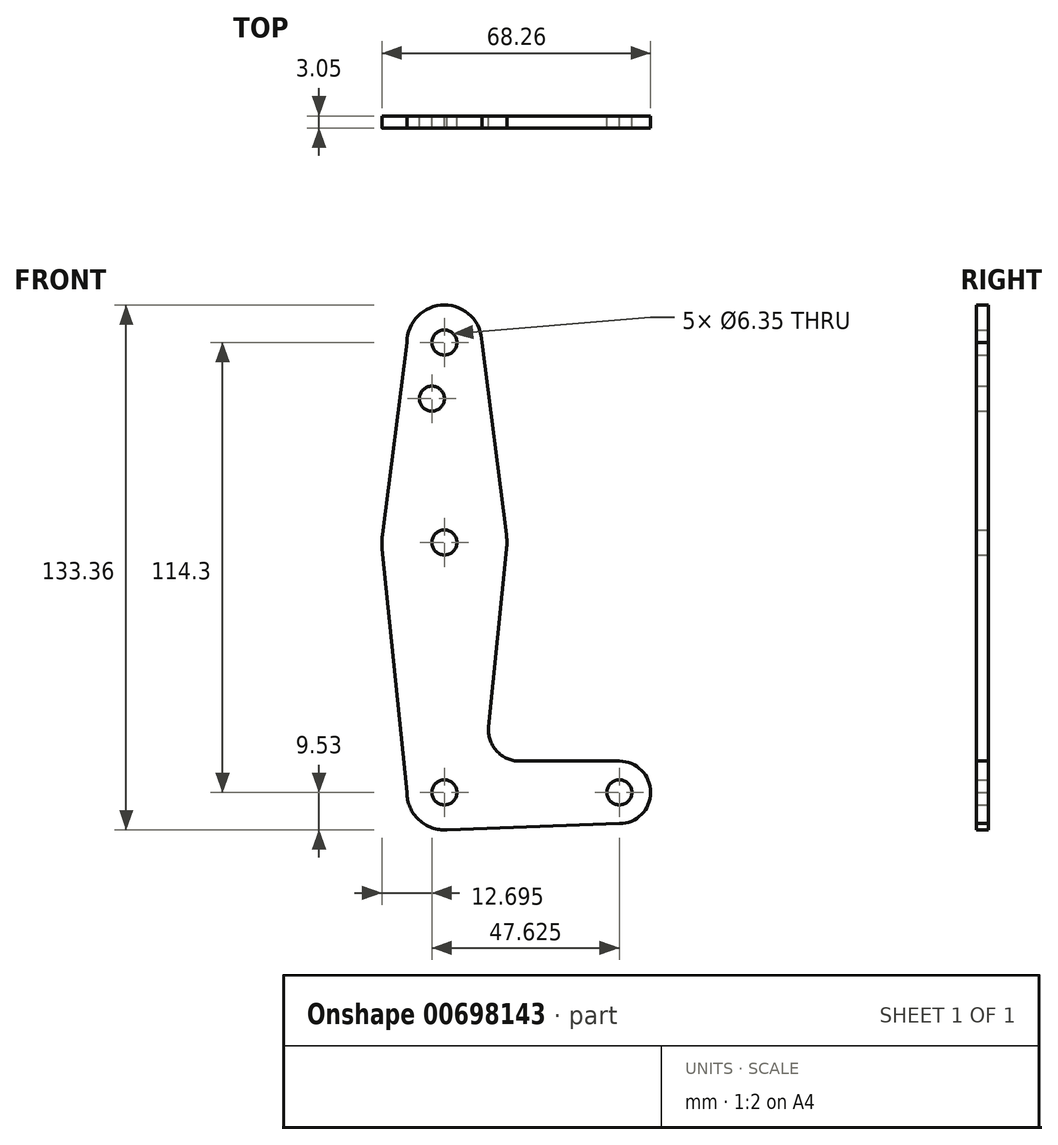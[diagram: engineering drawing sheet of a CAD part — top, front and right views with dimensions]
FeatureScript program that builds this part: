
annotation { "Feature Type Name" : "Feature", "Feature Type Description" : "" }
export const myFeature = defineFeature(function(context is Context, id is Id, definition is map)
    precondition{}
    {
        {
            var Q0;
            Q0=qCreatedBy(makeId("Front.planeOp"),FACE);
            var sketch = newSketch(context, id + "F0", { "sketchPlane" : qUnion([Q0])});
            skCircle(sketch, "E0", {"center": v(0, 0) * mm, "radius": 9.53 * mm});
            skLineSegment(sketch, "E1", {"start": v(0, 0) * mm, "end": v(0, 114.3) * mm});
            skCircle(sketch, "E2", {"center": v(0, 114.3) * mm, "radius": 9.53 * mm});
            skCircle(sketch, "E3", {"center": v(0, 63.5) * mm, "radius": 15.88 * mm});
            skCircle(sketch, "E4", {"center": v(44.45, 0) * mm, "radius": 7.94 * mm});
            skLineSegment(sketch, "E5", {"start": v(0, 0) * mm, "end": v(44.45, 0) * mm});
            skLineSegment(sketch, "E6", {"start": v(19.12, 7.94) * mm, "end": v(44.45, 7.94) * mm});
            skLineSegment(sketch, "E7", {"start": v(0, -9.52) * mm, "end": v(44.45, -7.94) * mm});
            skCircle(sketch, "E8", {"center": v(0, 114.3) * mm, "radius": 3.18 * mm});
            skCircle(sketch, "E9", {"center": v(0, 63.5) * mm, "radius": 3.18 * mm});
            skCircle(sketch, "E10", {"center": v(0, 0) * mm, "radius": 3.18 * mm});
            skCircle(sketch, "E11", {"center": v(44.45, 0) * mm, "radius": 3.18 * mm});
            skLineSegment(sketch, "E12", {"start": v(-9.53, 114.3) * mm, "end": v(-15.75, 65.5) * mm});
            skLineSegment(sketch, "E13", {"start": v(-9.53, 0) * mm, "end": v(-15.8, 61.9) * mm});
            skLineSegment(sketch, "E14", {"start": v(11.22, 16.69) * mm, "end": v(15.8, 61.9) * mm});
            skLineSegment(sketch, "E15", {"start": v(9.53, 114.3) * mm, "end": v(15.75, 65.5) * mm});
            skArc(sketch, "E16.filletArc", {"start": v(11.22, 16.69) * mm, "mid": v(13.23, 10.56) * mm, "end": v(19.12, 7.94) * mm});
            skCircle(sketch, "E17", {"center": v(-3.18, 100.03) * mm, "radius": 3.18 * mm});
            skSolve(sketch);
        }
        {
            var Q0;
            Q0 = qSketchRegion(id + "F0", true);
            var Q1;
            {var subQ0=sQuery(id+"F0.wireOp",EDGE,"E1");var subQ1=sQuery(id+"F0.wireOp",EDGE,"E0");var subQ2=makeQuery(id+"F0.imprint","INTERSECT",VERTEX,{"derivedFrom":[subQ1,subQ0]});Q1=makeQuery(id+"F0.imprint","IMPRINT",FACE,{"disambiguationData":[TD([[makeQuery(id+"F0.imprint","IMPRINT",EDGE,{"disambiguationData":[TD([[subQ2,1.0]])],"derivedFrom":subQ1}),1.0]])]});}
            extrude(context, id + "F1", {"entities" : qUnion([Q0, Q1]), "depth" : 3.05 * mm, "offsetDistance" : 25.4 * mm});
        }
    });
